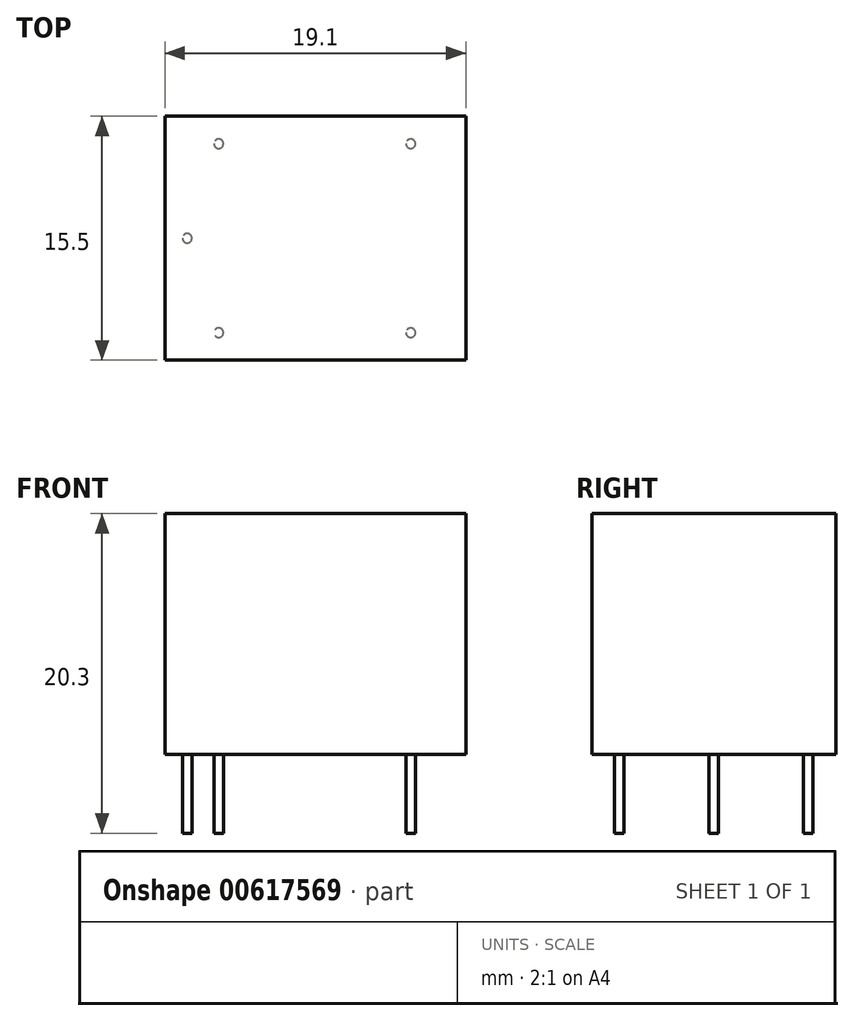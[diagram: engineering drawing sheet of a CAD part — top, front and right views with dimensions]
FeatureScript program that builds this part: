
annotation { "Feature Type Name" : "Feature", "Feature Type Description" : "" }
export const myFeature = defineFeature(function(context is Context, id is Id, definition is map)
    precondition{}
    {
        {
            var Q0;
            Q0=qCreatedBy(makeId("Top.planeOp"),FACE);
            var sketch = newSketch(context, id + "F0", { "sketchPlane" : qUnion([Q0])});
            skLineSegment(sketch, "E0.bottom", {"start": v(-9.55, 7.75) * mm, "end": v(9.55, 7.75) * mm});
            skLineSegment(sketch, "E0.top", {"start": v(-9.55, -7.75) * mm, "end": v(9.55, -7.75) * mm});
            skLineSegment(sketch, "E0.left", {"start": v(-9.55, 7.75) * mm, "end": v(-9.55, -7.75) * mm});
            skLineSegment(sketch, "E0.right", {"start": v(9.55, 7.75) * mm, "end": v(9.55, -7.75) * mm});
            skPoint(sketch, "E0.middle", {"position": v(0, 0) * mm});
            skSolve(sketch);
        }
        {
            var Q0;
            Q0 = qSketchRegion(id + "F0", true);
            extrude(context, id + "F1", {"entities" : qUnion([Q0]), "depth" : 15.3 * mm, "offsetDistance" : 25 * mm});
        }
        {
            var Q0;
            Q0=makeQuery(id+"F1.opExtrude","CAP_FACE",FACE,{"disambiguationData":[OSD([sQuery(id+"F0.wireOp",EDGE,"E0.bottom"),sQuery(id+"F0.wireOp",EDGE,"E0.top"),sQuery(id+"F0.wireOp",EDGE,"E0.left"),sQuery(id+"F0.wireOp",EDGE,"E0.right")])],"isStart":true});
            var sketch = newSketch(context, id + "F2", { "sketchPlane" : qUnion([Q0])});
            skCircle(sketch, "E1.MirrorC", {"center": v(-6.15, 6) * mm, "radius": 0.3 * mm});
            skCircle(sketch, "E2.MirrorC", {"center": v(-6.15, -6) * mm, "radius": 0.3 * mm});
            skCircle(sketch, "E3", {"center": v(-8.15, 0) * mm, "radius": 0.3 * mm});
            skCircle(sketch, "E4.1.0.0", {"center": v(6.05, 6) * mm, "radius": 0.3 * mm});
            skCircle(sketch, "E4.1.0.1", {"center": v(6.05, -6) * mm, "radius": 0.3 * mm});
            skLineSegment(sketch, "E4.direction1", {"start": v(-6.15, -6) * mm, "end": v(6.05, -6) * mm, "construction": true});
            skSolve(sketch);
        }
        {
            var Q0;
            Q0 = qSketchRegion(id + "F2", true);
            extrude(context, id + "F3", {"entities" : qUnion([Q0]), "operationType" : NewBodyOperationType.ADD, "depth" : 5 * mm, "offsetDistance" : 25 * mm});
        }
    });
